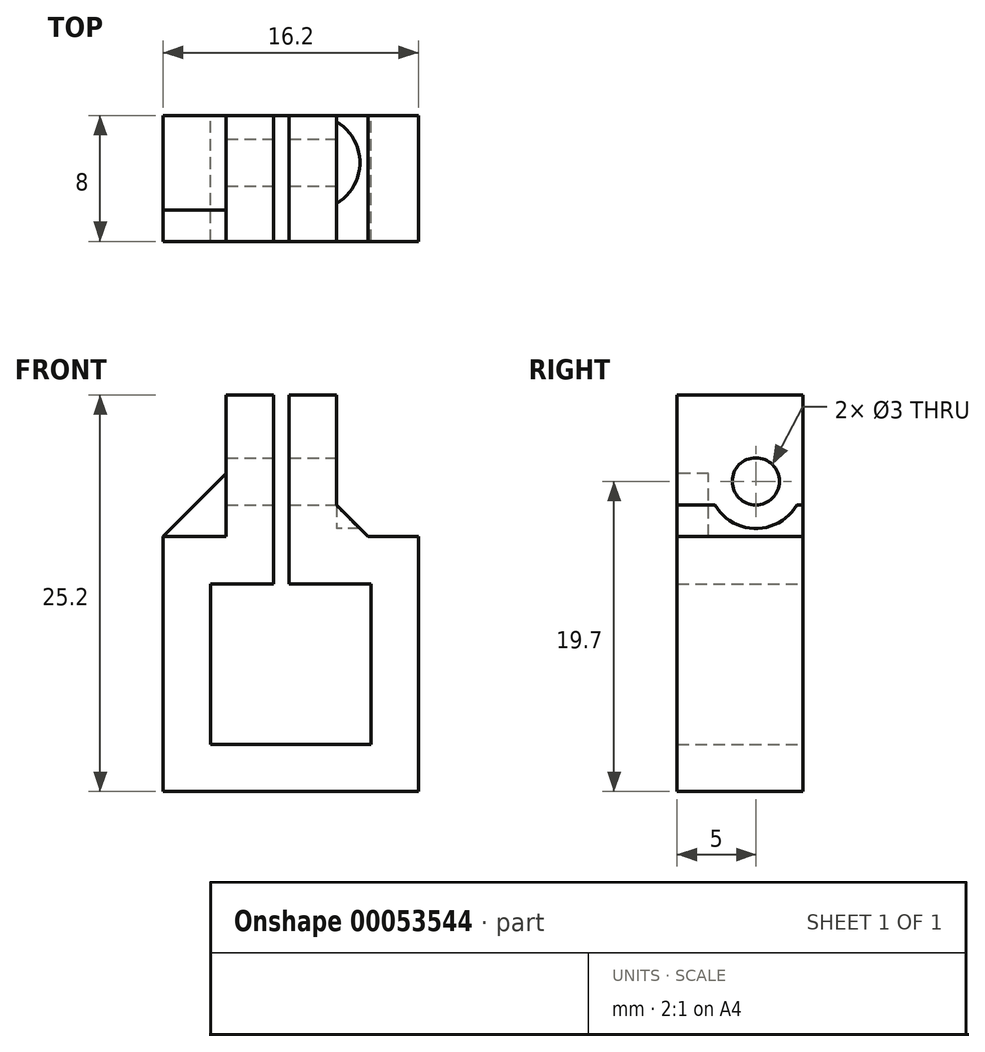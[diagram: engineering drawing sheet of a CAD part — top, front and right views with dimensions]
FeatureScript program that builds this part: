
annotation { "Feature Type Name" : "Feature", "Feature Type Description" : "" }
export const myFeature = defineFeature(function(context is Context, id is Id, definition is map)
    precondition{}
    {
        {
            var Q0;
            Q0=qCreatedBy(makeId("Front.planeOp"),FACE);
            var sketch = newSketch(context, id + "F0", { "sketchPlane" : qUnion([Q0])});
            skLineSegment(sketch, "E0.rect.bottom", {"start": v(5.1, -5.1) * mm, "end": v(-5.1, -5.1) * mm});
            skLineSegment(sketch, "E0.rect.top", {"start": v(5.1, 5.1) * mm, "end": v(-0.1, 5.1) * mm});
            skLineSegment(sketch, "E0.rect.left", {"start": v(5.1, -5.1) * mm, "end": v(5.1, 5.1) * mm});
            skLineSegment(sketch, "E0.rect.right", {"start": v(-5.1, -5.1) * mm, "end": v(-5.1, 5.1) * mm});
            skPoint(sketch, "E0.rect.middle", {"position": v(0, 0) * mm});
            skLineSegment(sketch, "E1.0", {"start": v(8.1, 8.1) * mm, "end": v(2.9, 8.1) * mm});
            skLineSegment(sketch, "E1.1", {"start": v(8.1, -8.1) * mm, "end": v(8.1, 8.1) * mm});
            skLineSegment(sketch, "E1.2", {"start": v(8.1, -8.1) * mm, "end": v(-8.1, -8.1) * mm});
            skLineSegment(sketch, "E1.3", {"start": v(-8.1, -8.1) * mm, "end": v(-8.1, 8.1) * mm});
            skLineSegment(sketch, "E2", {"start": v(-4.1, 8.1) * mm, "end": v(-4.1, 17.1) * mm});
            skLineSegment(sketch, "E3", {"start": v(-4.1, 17.1) * mm, "end": v(-1.1, 17.1) * mm});
            skLineSegment(sketch, "E4", {"start": v(-1.1, 17.1) * mm, "end": v(-1.1, 8.1) * mm});
            skLineSegment(sketch, "E5", {"start": v(-0.1, 17.1) * mm, "end": v(-0.1, 8.1) * mm});
            skLineSegment(sketch, "E6", {"start": v(-0.1, 17.1) * mm, "end": v(2.9, 17.1) * mm});
            skLineSegment(sketch, "E7", {"start": v(2.9, 17.1) * mm, "end": v(2.9, 8.1) * mm});
            skLineSegment(sketch, "E8", {"start": v(-4.1, 8.1) * mm, "end": v(-5.1, 8.1) * mm});
            skLineSegment(sketch, "E9", {"start": v(-8.1, 8.1) * mm, "end": v(-4.1, 8.1) * mm});
            skPoint(sketch, "E10.end.orphan", {"position": v(-5.1, 17.1) * mm});
            skLineSegment(sketch, "E11", {"start": v(-4.1, 5.1) * mm, "end": v(-5.1, 5.1) * mm});
            skLineSegment(sketch, "E12", {"start": v(-1.1, 8.1) * mm, "end": v(-1.1, 5.1) * mm});
            skLineSegment(sketch, "E13", {"start": v(-0.1, 8.1) * mm, "end": v(-0.1, 5.1) * mm});
            skPoint(sketch, "E13.endSnap0", {"position": v(0.5, 5.1) * mm});
            skLineSegment(sketch, "E14.trimOffspring", {"start": v(-1.1, 5.1) * mm, "end": v(-4.1, 5.1) * mm});
            skSolve(sketch);
        }
        {
            var Q0;
            Q0=qSketchRegion(id+"F0",true);
            extrude(context, id + "F1", {"entities" : qUnion([Q0]), "depth" : 8 * mm});
        }
        {
            var Q0;
            Q0=makeQuery(id+"F1.opExtrude","SWEPT_FACE",FACE,{"disambiguationData":[OSD([sQuery(id+"F0.wireOp",EDGE,"E4")])]});
            var sketch = newSketch(context, id + "F2", { "sketchPlane" : qUnion([Q0])});
            skCircle(sketch, "E15", {"center": v(-3, 11.6) * mm, "radius": 1.5 * mm});
            skPoint(sketch, "E15.centerSnap0", {"position": v(-7, 11.6) * mm});
            skPoint(sketch, "E15.centerSnap1", {"position": v(-3, 16.1) * mm});
            skSolve(sketch);
        }
        {
            var Q0;
            Q0=qSketchRegion(id+"F2",true);
            extrude(context, id + "F3", {"entities" : qUnion([Q0]), "operationType" : NewBodyOperationType.REMOVE, "oppositeDirection" : true, "depth" : 25 * mm, "symmetric" : true});
        }
        {
            var Q0;
            Q0=makeQuery(id+"F1.opExtrude","SWEPT_EDGE",EDGE,{"disambiguationData":[OSD([sQuery(id+"F0.wireOp",EDGE,"E1.0"),sQuery(id+"F0.wireOp",EDGE,"E7")])]});
            chamfer(context, id + "F4", {"entities" : qUnion([Q0]), "width" : 2 * mm, "tangentPropagation" : true});
        }
        {
            var Q0;
            Q0=makeQuery(id+"F1.opExtrude","SWEPT_FACE",FACE,{"disambiguationData":[OSD([sQuery(id+"F0.wireOp",EDGE,"E7")])]});
            var sketch = newSketch(context, id + "F5", { "sketchPlane" : qUnion([Q0])});
            skCircle(sketch, "E16", {"center": v(-3, 11.6) * mm, "radius": 3 * mm});
            skSolve(sketch);
        }
        {
            var Q0;
            Q0 = qSketchRegion(id + "F5", true);
            extrude(context, id + "F6", {"entities" : qUnion([Q0]), "operationType" : NewBodyOperationType.REMOVE, "depth" : 4 * mm});
        }
        {
            var Q0;
            Q0=makeQuery(id+"F1.opExtrude","CAP_FACE",FACE,{"disambiguationData":[OSD([sQuery(id+"F0.wireOp",EDGE,"E0.rect.bottom"),sQuery(id+"F0.wireOp",EDGE,"E0.rect.top"),sQuery(id+"F0.wireOp",EDGE,"E0.rect.left"),sQuery(id+"F0.wireOp",EDGE,"E0.rect.right"),sQuery(id+"F0.wireOp",EDGE,"E1.0"),sQuery(id+"F0.wireOp",EDGE,"E1.1"),sQuery(id+"F0.wireOp",EDGE,"E1.2"),sQuery(id+"F0.wireOp",EDGE,"E1.3"),sQuery(id+"F0.wireOp",EDGE,"E2"),sQuery(id+"F0.wireOp",EDGE,"E3"),sQuery(id+"F0.wireOp",EDGE,"E4"),sQuery(id+"F0.wireOp",EDGE,"E5"),sQuery(id+"F0.wireOp",EDGE,"E6"),sQuery(id+"F0.wireOp",EDGE,"E7"),sQuery(id+"F0.wireOp",EDGE,"E9"),sQuery(id+"F0.wireOp",EDGE,"E11"),sQuery(id+"F0.wireOp",EDGE,"E12"),sQuery(id+"F0.wireOp",EDGE,"E13"),sQuery(id+"F0.wireOp",EDGE,"E14.trimOffspring")])],"isStart":false});
            var sketch = newSketch(context, id + "F7", { "sketchPlane" : qUnion([Q0])});
            skLineSegment(sketch, "E17", {"start": v(-8.1, 8.1) * mm, "end": v(-4.1, 12.1) * mm});
            skLineSegment(sketch, "E18", {"start": v(-8.1, 8.1) * mm, "end": v(-4.1, 8.1) * mm});
            skLineSegment(sketch, "E19", {"start": v(-4.1, 8.1) * mm, "end": v(-4.1, 12.1) * mm});
            skSolve(sketch);
        }
        {
            var Q0;
            Q0 = qSketchRegion(id + "F7", true);
            extrude(context, id + "F8", {"entities" : qUnion([Q0]), "oppositeDirection" : true, "depth" : 2 * mm});
        }
    });
